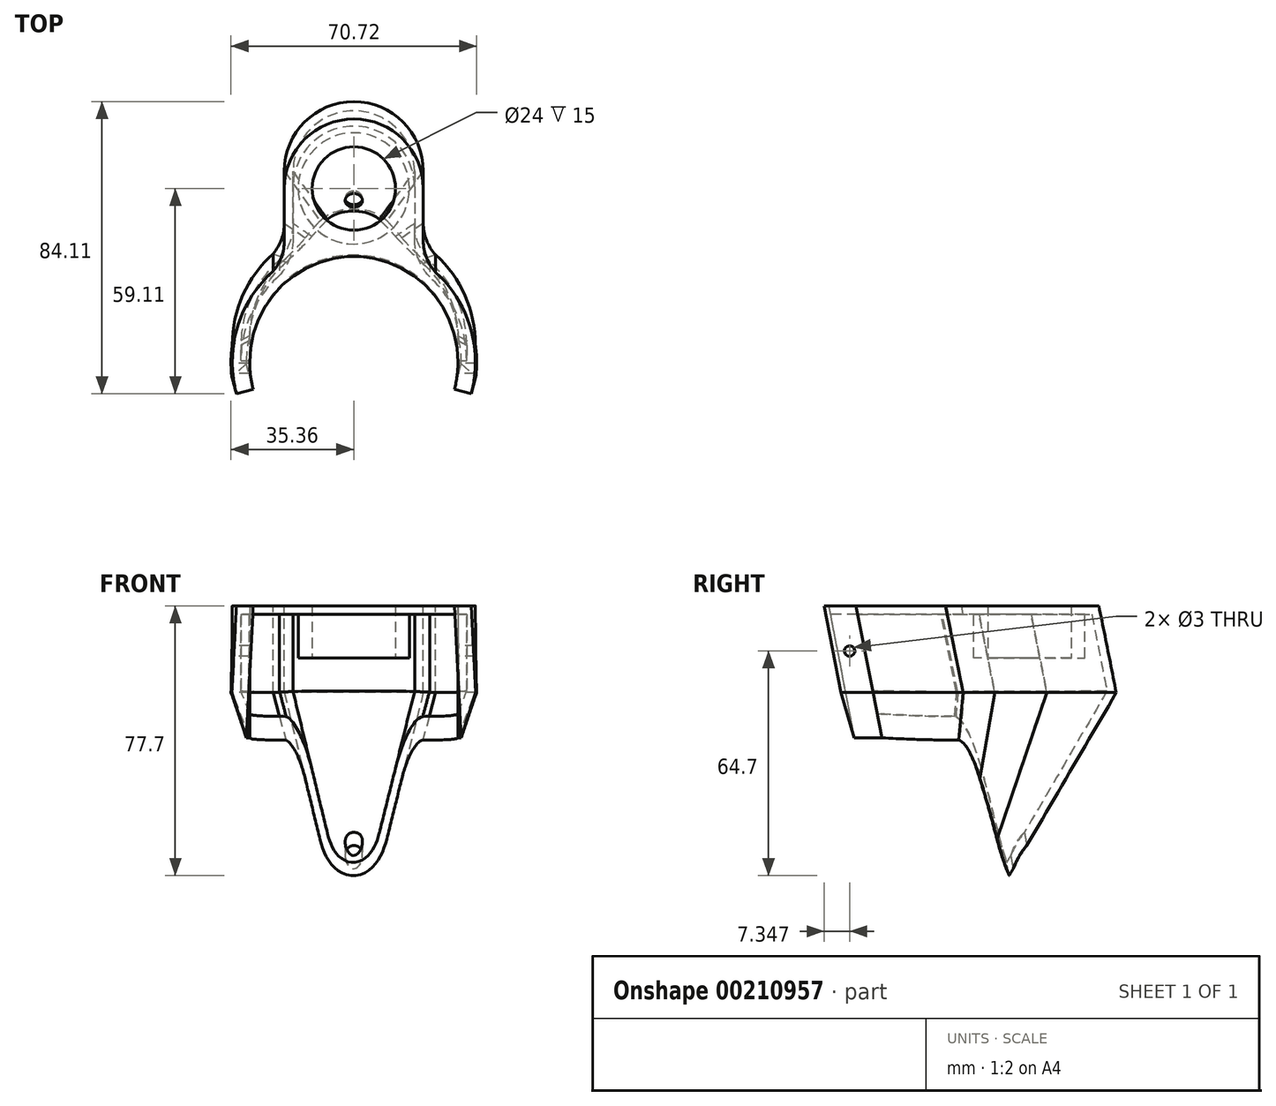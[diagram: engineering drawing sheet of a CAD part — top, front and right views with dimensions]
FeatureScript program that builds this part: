
annotation { "Feature Type Name" : "Feature", "Feature Type Description" : "" }
export const myFeature = defineFeature(function(context is Context, id is Id, definition is map)
    precondition{}
    {
        {
            var Q0;
            Q0=qCreatedBy(makeId("Top.planeOp"),FACE);
            var sketch = newSketch(context, id + "F0", { "sketchPlane" : qUnion([Q0])});
            skArc(sketch, "E0", {"start": v(35, 0) * mm, "mid": v(0, 35) * mm, "end": v(-35, 0) * mm, "construction": true});
            skLineSegment(sketch, "E1", {"start": v(-20, 50) * mm, "end": v(-20, 35) * mm});
            skLineSegment(sketch, "E2", {"start": v(20, 50) * mm, "end": v(20, 35) * mm});
            skLineSegment(sketch, "E3", {"start": v(-35, 0) * mm, "end": v(35, 0) * mm});
            skArc(sketch, "E4", {"start": v(20, 35) * mm, "mid": v(20.93, 30.1) * mm, "end": v(23.58, 25.87) * mm});
            skArc(sketch, "E5", {"start": v(20, 50) * mm, "mid": v(0, 70) * mm, "end": v(-20, 50) * mm});
            skArc(sketch, "E6", {"start": v(-23.2, 26.2) * mm, "mid": v(-20.83, 30.32) * mm, "end": v(-20, 35) * mm});
            skArc(sketch, "E7", {"start": v(-23.2, 26.2) * mm, "mid": v(-31.91, 14.37) * mm, "end": v(-35, 0) * mm});
            skArc(sketch, "E8", {"start": v(35, 0) * mm, "mid": v(32.02, 14.14) * mm, "end": v(23.58, 25.87) * mm});
            skSolve(sketch);
        }
        {
            var Q0;
            Q0=qCreatedBy(makeId("Top.planeOp"),FACE);
            cPlane(context, id + "F1", {"entities" : qUnion([Q0]), "cplaneType" : CPlaneType.OFFSET, "offset" : 25 * mm, "oppositeDirection" : true, "width" : 150 * mm, "height" : 150 * mm});
        }
        {
            var Q0;
            Q0=qCreatedBy(id+"F1.planeOp",FACE);
            var sketch = newSketch(context, id + "F2", { "sketchPlane" : qUnion([Q0])});
            skArc(sketch, "E9", {"start": v(35, 5) * mm, "mid": v(0, 40) * mm, "end": v(-35, 5) * mm, "construction": true});
            skLineSegment(sketch, "E10", {"start": v(-20, 55) * mm, "end": v(-20, 40) * mm});
            skLineSegment(sketch, "E11", {"start": v(20, 55) * mm, "end": v(20, 40) * mm});
            skLineSegment(sketch, "E12", {"start": v(-35, 5) * mm, "end": v(35, 5) * mm});
            skArc(sketch, "E13", {"start": v(20, 40) * mm, "mid": v(20.93, 35.1) * mm, "end": v(23.58, 30.87) * mm});
            skArc(sketch, "E14", {"start": v(20, 55) * mm, "mid": v(0, 75) * mm, "end": v(-20, 55) * mm});
            skArc(sketch, "E15", {"start": v(-23.2, 31.2) * mm, "mid": v(-20.83, 35.32) * mm, "end": v(-20, 40) * mm});
            skArc(sketch, "E16", {"start": v(-23.2, 31.2) * mm, "mid": v(-31.91, 19.37) * mm, "end": v(-35, 5) * mm});
            skArc(sketch, "E17", {"start": v(35, 5) * mm, "mid": v(32.02, 19.14) * mm, "end": v(23.58, 30.87) * mm});
            skSolve(sketch);
        }
        {
            var Q0;
            {var subQ0=sQuery(id+"F2.wireOp",EDGE,"E12");Q0=makeQuery(id+"F2.imprint","IMPRINT",FACE,{"disambiguationData":[TD([[makeQuery(id+"F2.imprint","IMPRINT",EDGE,{"derivedFrom":subQ0}),1.0]])]});}
            var Q1;
            {var subQ0=sQuery(id+"F0.wireOp",EDGE,"E3");Q1=makeQuery(id+"F0.imprint","IMPRINT",FACE,{"disambiguationData":[TD([[makeQuery(id+"F0.imprint","IMPRINT",EDGE,{"derivedFrom":subQ0}),1.0]])]});}
            loft(context, id + "F3", {"sheetProfilesArray" : [{ "sheetProfileEntities" : qUnion([Q0]) }, { "sheetProfileEntities" : qUnion([Q1]) }]});
        }
        {
            var Q0;
            Q0=makeQuery(id+"F2.imprint","IMPRINT",FACE,{"disambiguationData":[TD([[makeQuery(id+"F2.imprint","IMPRINT",EDGE,{"derivedFrom":sQuery(id+"F2.wireOp",EDGE,"E10")}),1.0]])]});
            var Q1;
            Q1=makeQuery(id+"F0.imprint","IMPRINT",FACE,{"disambiguationData":[TD([[makeQuery(id+"F0.imprint","IMPRINT",EDGE,{"derivedFrom":sQuery(id+"F0.wireOp",EDGE,"E1")}),1.0]])]});
            loft(context, id + "F4", {"operationType" : NewBodyOperationType.ADD, "sheetProfilesArray" : [{ "sheetProfileEntities" : qUnion([Q0]) }, { "sheetProfileEntities" : qUnion([Q1]) }]});
        }
        {
            var Q0;
            Q0=qCreatedBy(id+"F1.planeOp",FACE);
            cPlane(context, id + "F5", {"entities" : qUnion([Q0]), "cplaneType" : CPlaneType.OFFSET, "offset" : 65 * mm, "oppositeDirection" : true, "width" : 150 * mm, "height" : 150 * mm});
        }
        {
            var Q0;
            Q0=qCreatedBy(id+"F5.planeOp",FACE);
            var sketch = newSketch(context, id + "F6", { "sketchPlane" : qUnion([Q0])});
            skArc(sketch, "E18", {"start": v(10, 16.96) * mm, "mid": v(0, 26.97) * mm, "end": v(-10, 16.97) * mm, "construction": true});
            skLineSegment(sketch, "E19", {"start": v(-10, 16.97) * mm, "end": v(10, 16.96) * mm});
            skArc(sketch, "E20", {"start": v(3.79, 32.96) * mm, "mid": v(-0.21, 36.96) * mm, "end": v(-4.21, 32.96) * mm});
            skLineSegment(sketch, "E21", {"start": v(-4.21, 32.96) * mm, "end": v(-4.21, 28.96) * mm});
            skLineSegment(sketch, "E22", {"start": v(3.79, 32.96) * mm, "end": v(3.79, 28.96) * mm});
            skArc(sketch, "E23", {"start": v(-6, 24.97) * mm, "mid": v(-4.68, 26.77) * mm, "end": v(-4.21, 28.96) * mm});
            skArc(sketch, "E24", {"start": v(3.79, 28.96) * mm, "mid": v(4.38, 26.68) * mm, "end": v(6, 24.97) * mm});
            skArc(sketch, "E25", {"start": v(-6, 24.97) * mm, "mid": v(-8.94, 21.44) * mm, "end": v(-10, 16.97) * mm});
            skArc(sketch, "E26", {"start": v(10, 16.96) * mm, "mid": v(8.95, 21.44) * mm, "end": v(6, 24.97) * mm});
            skSolve(sketch);
        }
        {
            var Q1;
            Q1=makeQuery(id+"F2.imprint","IMPRINT",FACE,{"disambiguationData":[TD([[makeQuery(id+"F2.imprint","IMPRINT",EDGE,{"derivedFrom":sQuery(id+"F2.wireOp",EDGE,"E10")}),1.0]])]});
            var Q2;
            Q2=makeQuery(id+"F6.imprint","IMPRINT",FACE,{"disambiguationData":[TD([[makeQuery(id+"F6.imprint","IMPRINT",EDGE,{"derivedFrom":sQuery(id+"F6.wireOp",EDGE,"E19")}),1.0]])]});
            loft(context, id + "F7", {"operationType" : NewBodyOperationType.ADD, "sheetProfilesArray" : [{ "sheetProfileEntities" : qUnion([Q1]) }, { "sheetProfileEntities" : qUnion([Q2]) }]});
        }
        {
            var Q0;
            Q0=makeQuery(id+"F7.opLoft","SWEPT_FACE",FACE,{"disambiguationData":[OSD([sQuery(id+"F2.wireOp",EDGE,"E12"),sQuery(id+"F2.wireOp",EDGE,"E16"),sQuery(id+"F2.wireOp",EDGE,"E17"),sQuery(id+"F6.wireOp",EDGE,"E19"),sQuery(id+"F6.wireOp",EDGE,"E25"),sQuery(id+"F6.wireOp",EDGE,"E26")])]});
            var Q1;
            Q1=makeQuery(id+"F3.opLoft","SWEPT_FACE",FACE,{"disambiguationData":[OSD([sQuery(id+"F0.wireOp",EDGE,"E3"),sQuery(id+"F0.wireOp",EDGE,"E7"),sQuery(id+"F0.wireOp",EDGE,"E8"),sQuery(id+"F2.wireOp",EDGE,"E12"),sQuery(id+"F2.wireOp",EDGE,"E16"),sQuery(id+"F2.wireOp",EDGE,"E17")])]});
            shell(context, id + "F8", {"entities" : qUnion([Q0, Q1]), "thickness" : 2.5 * mm});
        }
        {
            var Q0;
            Q0=qCreatedBy(makeId("Top.planeOp"),FACE);
            var Q1;
            Q1=makeQuery(id+"F4.opLoft","MID_CAP_EDGE",EDGE,{"disambiguationData":[OSD([sQuery(id+"F0.wireOp",EDGE,"E0"),sQuery(id+"F0.wireOp",EDGE,"E3")])],"capPos":0.0});
            var Q2;
            Q2=sQuery(id+"F0.wireOp",EDGE,"E3");
            cPlane(context, id + "F9", {"entities" : qUnion([Q0, Q1, Q2]), "cplaneType" : CPlaneType.LINE_ANGLE, "offset" : 25 * mm, "angle" : 190 * degree, "width" : 150 * mm, "height" : 150 * mm});
        }
        {
            var Q0;
            Q0=qCreatedBy(id+"F9.planeOp",FACE);
            var sketch = newSketch(context, id + "F10", { "sketchPlane" : qUnion([Q0])});
            skCircle(sketch, "E27", {"center": v(0, 0) * mm, "radius": 30 * mm});
            skSolve(sketch);
        }
        {
            var Q0;
            Q0=makeQuery(id+"F10.imprint","IMPRINT",FACE,{"disambiguationData":[TD([[makeQuery(id+"F10.imprint","IMPRINT",EDGE,{"derivedFrom":sQuery(id+"F10.wireOp",EDGE,"E27")}),1.0]])]});
            extrude(context, id + "F11", {"entities" : qUnion([Q0]), "operationType" : NewBodyOperationType.REMOVE, "oppositeDirection" : true, "depth" : 100 * mm});
        }
        {
            var Q0;
            Q0=makeQuery(id+"F8.opShell","OFFSET_FACE",FACE,{"disambiguationData":[OSD([makeQuery(id+"F0.imprint","IMPRINT",FACE,{"disambiguationData":[TD([[makeQuery(id+"F0.imprint","IMPRINT",EDGE,{"derivedFrom":sQuery(id+"F0.wireOp",EDGE,"E1")}),1.0]])]})])]});
            var sketch = newSketch(context, id + "F12", { "sketchPlane" : qUnion([Q0])});
            skCircle(sketch, "E28", {"center": v(0, -50) * mm, "radius": 12 * mm});
            skSolve(sketch);
        }
        {
            var Q0;
            Q0=makeQuery(id+"F12.imprint","IMPRINT",FACE,{"disambiguationData":[TD([[makeQuery(id+"F12.imprint","IMPRINT",EDGE,{"derivedFrom":sQuery(id+"F12.wireOp",EDGE,"E28")}),1.0]])]});
            extrude(context, id + "F13", {"entities" : qUnion([Q0]), "operationType" : NewBodyOperationType.REMOVE, "oppositeDirection" : true, "depth" : 5 * mm});
        }
        {
            var Q0;
            Q0=makeQuery(id+"F8.opShell","OFFSET_FACE",FACE,{"disambiguationData":[OSD([makeQuery(id+"F0.imprint","IMPRINT",FACE,{"disambiguationData":[TD([[makeQuery(id+"F0.imprint","IMPRINT",EDGE,{"derivedFrom":sQuery(id+"F0.wireOp",EDGE,"E1")}),1.0]])]})])]});
            var sketch = newSketch(context, id + "F14", { "sketchPlane" : qUnion([Q0])});
            skCircle(sketch, "E29", {"center": v(0, -50) * mm, "radius": 12 * mm});
            skCircle(sketch, "E30", {"center": v(0, -50) * mm, "radius": 16 * mm});
            skSolve(sketch);
        }
        {
            var Q0;
            Q0=makeQuery(id+"F14.imprint","IMPRINT",FACE,{"disambiguationData":[TD([[makeQuery(id+"F14.imprint","IMPRINT",EDGE,{"derivedFrom":sQuery(id+"F14.wireOp",EDGE,"E29")}),-1.0]])]});
            extrude(context, id + "F15", {"entities" : qUnion([Q0]), "operationType" : NewBodyOperationType.ADD, "depth" : 12.5 * mm});
        }
        {
            var Q0;
            Q0=makeQuery(id+"F3.opLoft","CAP_FACE",FACE,{"disambiguationData":[OSD([makeQuery(id+"F0.imprint","IMPRINT",FACE,{"disambiguationData":[TD([[makeQuery(id+"F0.imprint","IMPRINT",EDGE,{"derivedFrom":sQuery(id+"F0.wireOp",EDGE,"E1")}),1.0]])]})])],"isStart":true});
            var sketch = newSketch(context, id + "F16", { "sketchPlane" : qUnion([Q0])});
            skArc(sketch, "E31", {"start": v(-32.5, 0) * mm, "mid": v(-32.22, -4.27) * mm, "end": v(-31.38, -8.46) * mm});
            skLineSegment(sketch, "E32", {"start": v(0, 0) * mm, "end": v(0, -28.86) * mm});
            skArc(sketch, "E33.MirrorCS", {"start": v(32.5, 0) * mm, "mid": v(32.22, -4.27) * mm, "end": v(31.38, -8.46) * mm});
            skSolve(sketch);
        }
        {
            var Q0;
            {var subQ3=sQuery(id+"F2.wireOp",EDGE,"E16");var subQ4=sQuery(id+"F2.wireOp",EDGE,"E15");var subQ5=sQuery(id+"F2.wireOp",EDGE,"E12");var subQ6=sQuery(id+"F2.wireOp",EDGE,"E17");var subQ7=sQuery(id+"F0.wireOp",EDGE,"E7");var subQ8=sQuery(id+"F0.wireOp",EDGE,"E6");var subQ9=sQuery(id+"F0.wireOp",EDGE,"E3");var subQ10=sQuery(id+"F0.wireOp",EDGE,"E8");Q0=makeQuery(id+"F11.boolean.opBoolean","SPLIT",FACE,{"disambiguationData":[TD([makeQuery(id+"F3.opLoft","SWEPT_FACE",FACE,{"disambiguationData":[OSD([subQ9,subQ8,subQ7,subQ5,subQ4,subQ3])]})])],"derivedFrom":makeQuery(id+"F3.opLoft","SWEPT_FACE",FACE,{"disambiguationData":[OSD([subQ9,subQ7,subQ10,subQ5,subQ3,subQ6])]})});}
            var sketch = newSketch(context, id + "F17", { "sketchPlane" : qUnion([Q0])});
            skLineSegment(sketch, "E34", {"start": v(-30, 0) * mm, "end": v(-30, -38.76) * mm});
            skLineSegment(sketch, "E35", {"start": v(-30, -38.76) * mm, "end": v(-35, -25.5) * mm});
            skLineSegment(sketch, "E36", {"start": v(-35, -25.5) * mm, "end": v(-35, 0) * mm});
            skLineSegment(sketch, "E37", {"start": v(-35, 0) * mm, "end": v(-30, 0) * mm});
            skLineSegment(sketch, "E38", {"start": v(0, 0) * mm, "end": v(0, -65.6) * mm});
            skLineSegment(sketch, "E39.MirrorCS", {"start": v(30, 0) * mm, "end": v(30, -38.76) * mm});
            skLineSegment(sketch, "E40.MirrorCS", {"start": v(30, -38.76) * mm, "end": v(35, -25.5) * mm});
            skLineSegment(sketch, "E41.MirrorCS", {"start": v(35, -25.5) * mm, "end": v(35, 0) * mm});
            skLineSegment(sketch, "E42.MirrorCS", {"start": v(35, 0) * mm, "end": v(30, 0) * mm});
            skSolve(sketch);
        }
        {
            var Q0;
            Q0=makeQuery(id+"F17.imprint","IMPRINT",FACE,{"disambiguationData":[TD([[makeQuery(id+"F17.imprint","IMPRINT",EDGE,{"derivedFrom":sQuery(id+"F17.wireOp",EDGE,"E39.MirrorCS")}),1.0]])]});
            var Q1;
            Q1=sQuery(id+"F16.wireOp",EDGE,"E33.MirrorCS");
            sweep(context, id + "F18", {"operationType" : NewBodyOperationType.ADD, "profiles" : qUnion([Q0]), "path" : qUnion([Q1])});
        }
        {
            var Q0;
            {var subQ8=sQuery(id+"F17.wireOp",EDGE,"E35");Q0=makeQuery(id+"F17.imprint","IMPRINT",FACE,{"disambiguationData":[TD([[makeQuery(id+"F17.imprint","IMPRINT",EDGE,{"derivedFrom":subQ8}),-1.0]])]});}
            var Q1;
            Q1=makeQuery(id+"F17.imprint","IMPRINT",FACE,{"disambiguationData":[TD([[makeQuery(id+"F17.imprint","IMPRINT",EDGE,{"derivedFrom":sQuery(id+"F17.wireOp",EDGE,"E36")}),1.0]])]});
            var Q2;
            Q2=sQuery(id+"F16.wireOp",EDGE,"E31");
            sweep(context, id + "F19", {"operationType" : NewBodyOperationType.ADD, "profiles" : qUnion([Q0, Q1]), "path" : qUnion([Q2])});
        }
        {
            var Q0;
            Q0=qCreatedBy(id+"F9.planeOp",FACE);
            cPlane(context, id + "F20", {"entities" : qUnion([Q0]), "cplaneType" : CPlaneType.OFFSET, "offset" : 100 * mm, "oppositeDirection" : true, "width" : 150 * mm, "height" : 150 * mm});
        }
        {
            var Q0;
            Q0=qCreatedBy(id+"F20.planeOp",FACE);
            var sketch = newSketch(context, id + "F21", { "sketchPlane" : qUnion([Q0])});
            skCircle(sketch, "E43", {"center": v(0, 34) * mm, "radius": 2.5 * mm});
            skSolve(sketch);
        }
        {
            var Q0;
            Q0=makeQuery(id+"F21.imprint","IMPRINT",FACE,{"disambiguationData":[TD([[makeQuery(id+"F21.imprint","IMPRINT",EDGE,{"derivedFrom":sQuery(id+"F21.wireOp",EDGE,"E43")}),1.0]])]});
            extrude(context, id + "F22", {"entities" : qUnion([Q0]), "operationType" : NewBodyOperationType.REMOVE, "depth" : 30 * mm});
        }
        {
            var Q0;
            Q0=qCreatedBy(makeId("Right.planeOp"),FACE);
            cPlane(context, id + "F23", {"entities" : qUnion([Q0]), "cplaneType" : CPlaneType.OFFSET, "offset" : 40 * mm, "oppositeDirection" : true, "width" : 150 * mm, "height" : 150 * mm});
        }
        {
            var Q0;
            Q0=qCreatedBy(id+"F23.planeOp",FACE);
            var sketch = newSketch(context, id + "F24", { "sketchPlane" : qUnion([Q0])});
            skCircle(sketch, "E44", {"center": v(-1.76, -13) * mm, "radius": 1.5 * mm});
            skSolve(sketch);
        }
        {
            var Q0;
            Q0=makeQuery(id+"F24.imprint","IMPRINT",FACE,{"disambiguationData":[TD([[makeQuery(id+"F24.imprint","IMPRINT",EDGE,{"derivedFrom":sQuery(id+"F24.wireOp",EDGE,"E44")}),1.0]])]});
            extrude(context, id + "F25", {"entities" : qUnion([Q0]), "operationType" : NewBodyOperationType.REMOVE, "depth" : 100 * mm});
        }
    });
